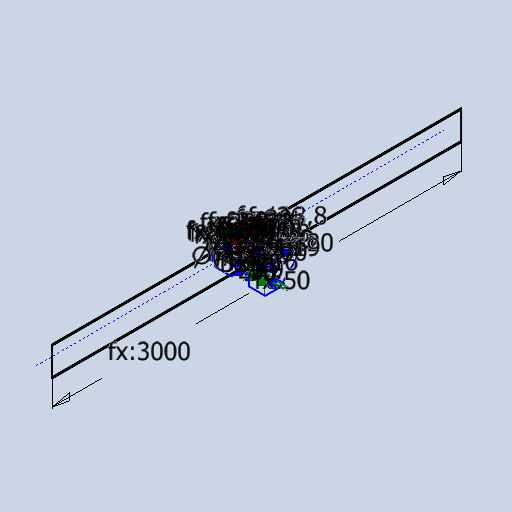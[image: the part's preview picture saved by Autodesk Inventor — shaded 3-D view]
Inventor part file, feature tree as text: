
AUTODESK INVENTOR PART (.ipt)
format: ipt  version: 2025.2 (Build 292293000, 293)  size: 464,896 bytes
history: native  units: mm
features: other x19, plane x12
ambient origin geometry x8: Origin, YZ Plane, XZ Plane, XY Plane, X Axis, Y Axis, Z Axis, Center Point
feature tree (31):
  other  "I_Traeger_front"
  other  "I_Traeger_seite"
  other  "Führungsplattenabstand"
  plane  "Arbeitsebene4"
  other  "Fuehrungsplatte_seite_Kettenzug"
  plane  "Arbeitsebene6"
  other  "Fuehrungsplatte_Laufradaufhängung_Kettenzug"
  plane  "Arbeitsebene7"
  other  "Fuehrungsplatte_Schraubbolzen_Kettenzug"
  plane  "Arbeitsebene8"
  other  "Laufrad"
  other  "Zahnrad_Laufrad_seite"
  plane  "Arbeitsebene9"
  other  "Zahnrad_Laufrad_front"
  plane  "Arbeitsebene10"
  other  "Fuehrungsplatte_seite_ohne"
  plane  "Arbeitsebene11"
  other  "Fuehrungsplatte_Laufradaufhängung_ohne"
  other  "Zahnrad_Zahnrad_seite"
  plane  "Arbeitsebene12"
  other  "Zahnrad_Zahnrad_front"
  plane  "Arbeitsebene13"
  other  "Fuehrungsplatte_Schraubbolzen_ohne"
  other  "Kettenzug_welle"
  plane  "Arbeitsebene15"
  other  "Kettenzug_scheibe_front"
  other  "Kettenzug_scheibe_seite"
  plane  "Arbeitsebene17"
  other  "Schraubbolzen_oben"
  plane  "Arbeitsebene18"
  other  "Schraubbolzen_Ankerausschnitt"
